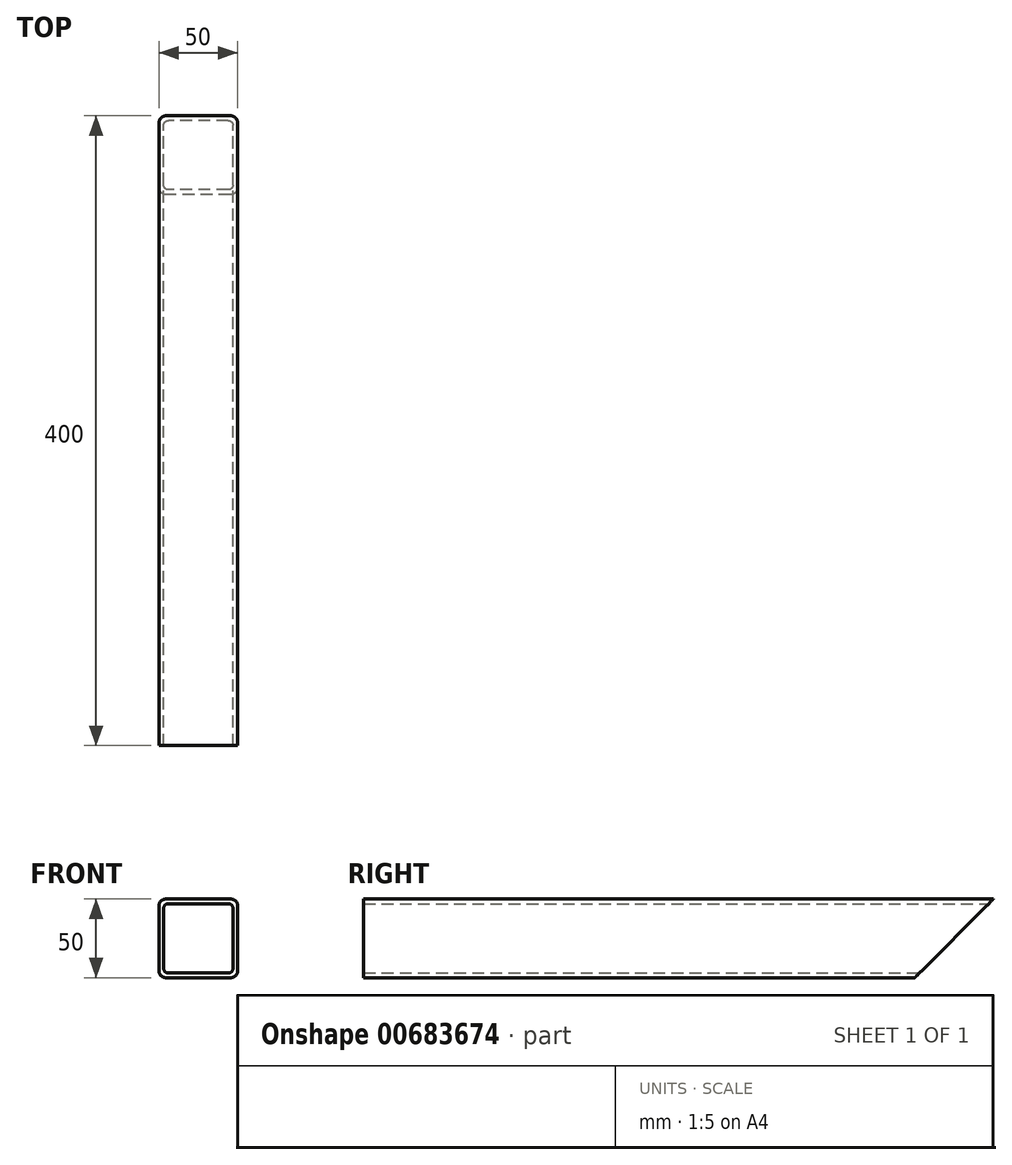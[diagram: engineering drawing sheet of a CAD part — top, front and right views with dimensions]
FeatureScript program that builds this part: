
annotation { "Feature Type Name" : "Feature", "Feature Type Description" : "" }
export const myFeature = defineFeature(function(context is Context, id is Id, definition is map)
    precondition{}
    {
        {
            var Q0;
            Q0=qCreatedBy(makeId("Front.planeOp"),FACE);
            var sketch = newSketch(context, id + "F0", { "sketchPlane" : qUnion([Q0])});
            skLineSegment(sketch, "E0.bottom", {"start": v(4.5, 0) * mm, "end": v(45.5, 0) * mm});
            skLineSegment(sketch, "E0.top", {"start": v(4.5, -50) * mm, "end": v(45.5, -50) * mm});
            skLineSegment(sketch, "E0.left", {"start": v(0, -4.5) * mm, "end": v(0, -45.5) * mm});
            skLineSegment(sketch, "E0.right", {"start": v(50, -4.5) * mm, "end": v(50, -45.5) * mm});
            skLineSegment(sketch, "E1.0", {"start": v(6, -3) * mm, "end": v(44, -3) * mm});
            skLineSegment(sketch, "E1.1", {"start": v(3, -6) * mm, "end": v(3, -44) * mm});
            skLineSegment(sketch, "E1.2", {"start": v(6, -47) * mm, "end": v(44, -47) * mm});
            skLineSegment(sketch, "E1.3", {"start": v(47, -6) * mm, "end": v(47, -44) * mm});
            skPoint(sketch, "E2.visualSharp", {"position": v(3, -3) * mm});
            skArc(sketch, "E2.filletArc", {"start": v(6, -3) * mm, "mid": v(3.88, -3.88) * mm, "end": v(3, -6) * mm});
            skPoint(sketch, "E3.visualSharp", {"position": v(47, -3) * mm});
            skArc(sketch, "E3.filletArc", {"start": v(47, -6) * mm, "mid": v(46.12, -3.88) * mm, "end": v(44, -3) * mm});
            skPoint(sketch, "E4.visualSharp", {"position": v(3, -47) * mm});
            skArc(sketch, "E4.filletArc", {"start": v(3, -44) * mm, "mid": v(3.88, -46.12) * mm, "end": v(6, -47) * mm});
            skPoint(sketch, "E5.visualSharp", {"position": v(47, -47) * mm});
            skArc(sketch, "E5.filletArc", {"start": v(44, -47) * mm, "mid": v(46.12, -46.12) * mm, "end": v(47, -44) * mm});
            skPoint(sketch, "E6.visualSharp", {"position": v(0, 0) * mm});
            skArc(sketch, "E6.filletArc", {"start": v(4.5, 0) * mm, "mid": v(1.32, -1.32) * mm, "end": v(0, -4.5) * mm});
            skPoint(sketch, "E7.visualSharp", {"position": v(50, 0) * mm});
            skArc(sketch, "E7.filletArc", {"start": v(50, -4.5) * mm, "mid": v(48.68, -1.32) * mm, "end": v(45.5, 0) * mm});
            skPoint(sketch, "E8.visualSharp", {"position": v(50, -50) * mm});
            skArc(sketch, "E8.filletArc", {"start": v(45.5, -50) * mm, "mid": v(48.68, -48.68) * mm, "end": v(50, -45.5) * mm});
            skPoint(sketch, "E9.visualSharp", {"position": v(0, -50) * mm});
            skArc(sketch, "E9.filletArc", {"start": v(0, -45.5) * mm, "mid": v(1.32, -48.68) * mm, "end": v(4.5, -50) * mm});
            skSolve(sketch);
        }
        {
            var Q0;
            Q0=makeQuery(id+"F0.imprint","IMPRINT",FACE,{"disambiguationData":[TD([[makeQuery(id+"F0.imprint","IMPRINT",EDGE,{"derivedFrom":sQuery(id+"F0.wireOp",EDGE,"E0.bottom")}),-1.0]])]});
            extrude(context, id + "F1", {"entities" : qUnion([Q0]), "depth" : 400 * mm, "offsetDistance" : 25 * mm});
        }
        {
            var Q0;
            Q0=qCreatedBy(makeId("Right.planeOp"),FACE);
            var sketch = newSketch(context, id + "F2", { "sketchPlane" : qUnion([Q0])});
            skLineSegment(sketch, "E10.0", {"start": v(0, -4.5) * mm, "end": v(0, -45.5) * mm});
            skLineSegment(sketch, "E11", {"start": v(0, 0) * mm, "end": v(-70.71, -70.71) * mm});
            skLineSegment(sketch, "E12", {"start": v(-70.71, -70.71) * mm, "end": v(29.29, -70.71) * mm});
            skLineSegment(sketch, "E13", {"start": v(29.29, -70.71) * mm, "end": v(29.29, 0) * mm});
            skLineSegment(sketch, "E14", {"start": v(29.29, 0) * mm, "end": v(0, 0) * mm});
            skLineSegment(sketch, "E15.0", {"start": v(-400, -45.5) * mm, "end": v(0, -45.5) * mm});
            skLineSegment(sketch, "E16", {"start": v(-200, -45.5) * mm, "end": v(-200, 29.62) * mm, "construction": true});
            skSolve(sketch);
        }
        {
            var Q0;
            Q0=makeQuery(id+"F2.imprint","IMPRINT",FACE,{"disambiguationData":[TD([[makeQuery(id+"F2.imprint","IMPRINT",EDGE,{"derivedFrom":sQuery(id+"F2.wireOp",EDGE,"E11")}),1.0]])]});
            var Q1;
            Q1=makeQuery(id+"F2.imprint","IMPRINT",FACE,{"disambiguationData":[TD([[makeQuery(id+"F2.imprint","IMPRINT",EDGE,{"derivedFrom":sQuery(id+"F2.wireOp",EDGE,"15ab33b6-9afe-43a0-9707-05ed60fb16ef0.MirrorCS")}),-1.0]])]});
            extrude(context, id + "F3", {"entities" : qUnion([Q0, Q1]), "operationType" : NewBodyOperationType.REMOVE, "endBound" : BoundingType.THROUGH_ALL, "depth" : 25 * mm, "offsetDistance" : 25 * mm});
        }
    });
